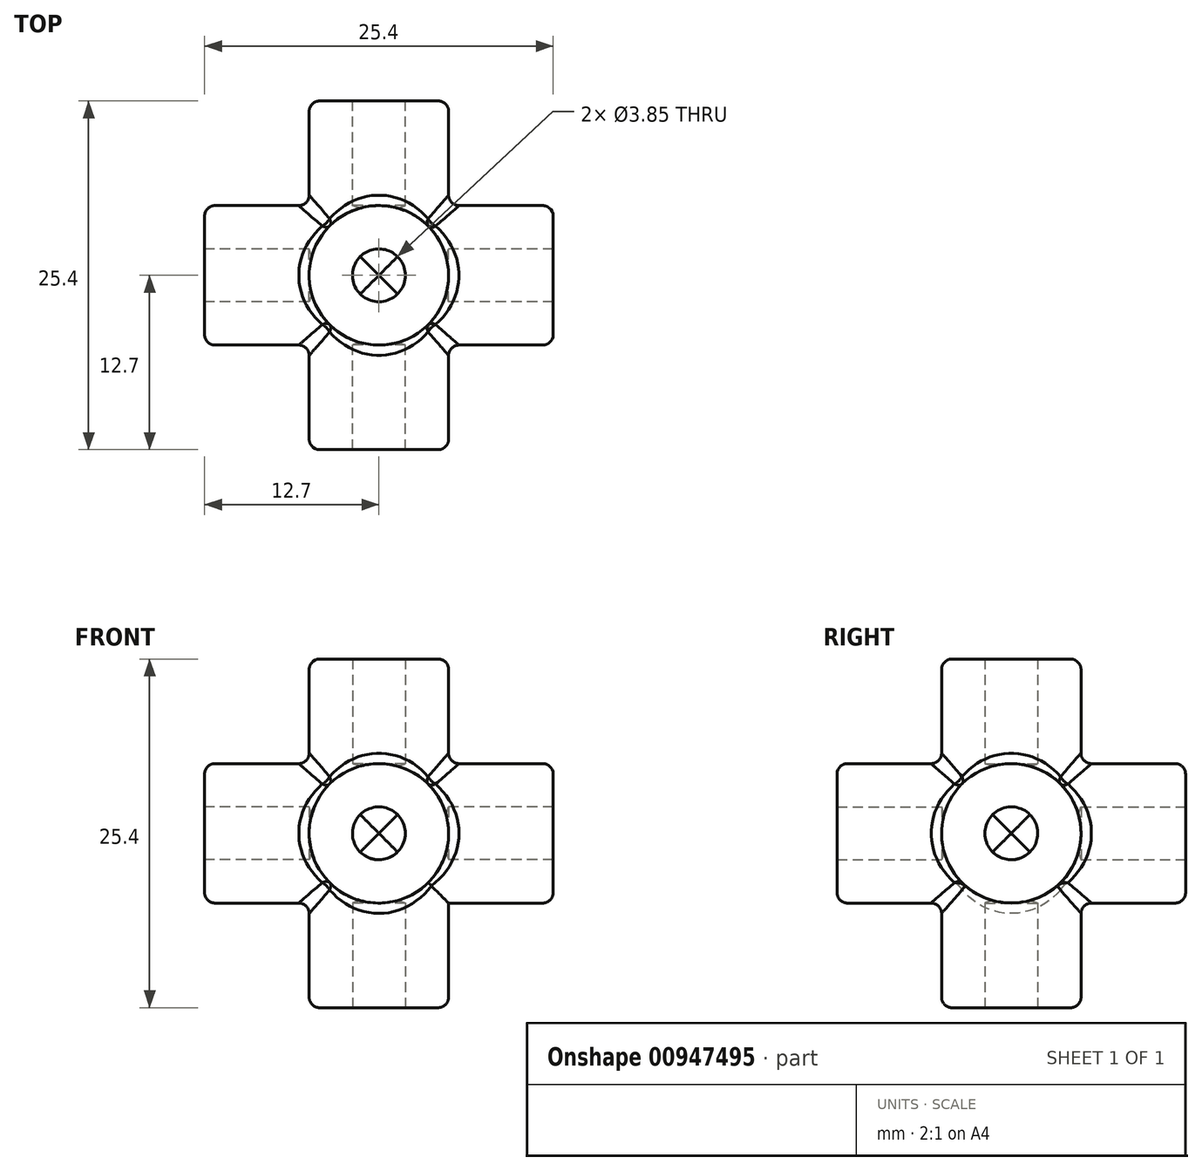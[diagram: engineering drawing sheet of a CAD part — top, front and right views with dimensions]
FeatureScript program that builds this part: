
annotation { "Feature Type Name" : "Feature", "Feature Type Description" : "" }
export const myFeature = defineFeature(function(context is Context, id is Id, definition is map)
    precondition{}
    {
        {
            var Q0;
            Q0=qCreatedBy(makeId("Front.planeOp"),FACE);
            var sketch = newSketch(context, id + "F0", { "sketchPlane" : qUnion([Q0])});
            skCircle(sketch, "E0", {"center": v(0, 0) * mm, "radius": 5.08 * mm});
            skCircle(sketch, "E1", {"center": v(0, 0) * mm, "radius": 1.92 * mm});
            skSolve(sketch);
        }
        {
            var Q0;
            Q0=makeQuery(id+"F0.imprint","IMPRINT",FACE,{"disambiguationData":[TD([[makeQuery(id+"F0.imprint","IMPRINT",EDGE,{"derivedFrom":sQuery(id+"F0.wireOp",EDGE,"E0")}),1.0]])]});
            extrude(context, id + "F1", {"entities" : qUnion([Q0]), "endBound" : BoundingType.SYMMETRIC, "depth" : 25.4 * mm, "offsetDistance" : 25.4 * mm});
        }
        {
            var Q0;
            Q0=qCreatedBy(makeId("Right.planeOp"),FACE);
            var sketch = newSketch(context, id + "F2", { "sketchPlane" : qUnion([Q0])});
            skCircle(sketch, "E2", {"center": v(0, 0) * mm, "radius": 1.92 * mm});
            skCircle(sketch, "E3", {"center": v(0, 0) * mm, "radius": 5.08 * mm});
            skSolve(sketch);
        }
        {
            var Q0;
            Q0=qCreatedBy(makeId("Top.planeOp"),FACE);
            var sketch = newSketch(context, id + "F3", { "sketchPlane" : qUnion([Q0])});
            skCircle(sketch, "E4", {"center": v(0, 0) * mm, "radius": 1.92 * mm});
            skCircle(sketch, "E5", {"center": v(0, 0) * mm, "radius": 5.08 * mm});
            skSolve(sketch);
        }
        {
            var Q0;
            Q0=qSketchRegion(id+"F2",true);
            extrude(context, id + "F4", {"entities" : qUnion([Q0]), "operationType" : NewBodyOperationType.ADD, "endBound" : BoundingType.SYMMETRIC, "depth" : 25.4 * mm, "offsetDistance" : 25.4 * mm});
        }
        {
            var Q0;
            Q0=makeQuery(id+"F3.imprint","IMPRINT",FACE,{"disambiguationData":[TD([[makeQuery(id+"F3.imprint","IMPRINT",EDGE,{"derivedFrom":sQuery(id+"F3.wireOp",EDGE,"E4")}),-1.0]])]});
            extrude(context, id + "F5", {"entities" : qUnion([Q0]), "operationType" : NewBodyOperationType.ADD, "endBound" : BoundingType.SYMMETRIC, "depth" : 25.4 * mm, "offsetDistance" : 25.4 * mm});
        }
        {
            var Q0;
            Q0=makeQuery(id+"F5.opExtrude","CAP_EDGE",EDGE,{"disambiguationData":[OSD([sQuery(id+"F3.wireOp",EDGE,"E5")])],"isStart":false});
            var Q1;
            Q1=makeQuery(id+"F1.opExtrude","CAP_EDGE",EDGE,{"disambiguationData":[OSD([sQuery(id+"F0.wireOp",EDGE,"E0")])],"isStart":false});
            var Q2;
            Q2=makeQuery(id+"F4.opExtrude","CAP_EDGE",EDGE,{"disambiguationData":[OSD([sQuery(id+"F2.wireOp",EDGE,"E3")])],"isStart":false});
            var Q3;
            Q3=makeQuery(id+"F1.opExtrude","CAP_EDGE",EDGE,{"disambiguationData":[OSD([sQuery(id+"F0.wireOp",EDGE,"E0")])],"isStart":true});
            var Q4;
            Q4=makeQuery(id+"F5.opExtrude","CAP_EDGE",EDGE,{"disambiguationData":[OSD([sQuery(id+"F3.wireOp",EDGE,"E5")])],"isStart":true});
            var Q5;
            Q5=makeQuery(id+"F4.opExtrude","CAP_EDGE",EDGE,{"disambiguationData":[OSD([sQuery(id+"F2.wireOp",EDGE,"E3")])],"isStart":true});
            var Q6;
            {var subQ0=sQuery(id+"F0.wireOp",EDGE,"E0");var subQ1=makeQuery(id+"F1.opExtrude","SWEPT_FACE",FACE,{"disambiguationData":[OSD([subQ0])]});Q6=makeQuery(id+"F5.boolean.opBoolean","INTERSECT",EDGE,{"disambiguationData":[OD(0.0)],"derivedFrom":[makeQuery(id+"F4.boolean.opBoolean","SPLIT",FACE,{"disambiguationData":[TD([subQ1,makeQuery(id+"F1.opExtrude","CAP_FACE",FACE,{"disambiguationData":[OSD([subQ0,sQuery(id+"F0.wireOp",EDGE,"E1")])],"isStart":true}),makeQuery(id+"F4.opExtrude","SWEPT_FACE",FACE,{"disambiguationData":[OSD([sQuery(id+"F2.wireOp",EDGE,"E3")])]})])],"derivedFrom":subQ1}),makeQuery(id+"F5.opExtrude","SWEPT_FACE",FACE,{"disambiguationData":[OSD([sQuery(id+"F3.wireOp",EDGE,"E5")])]})]});}
            var Q7;
            {var subQ0=sQuery(id+"F2.wireOp",EDGE,"E3");var subQ1=makeQuery(id+"F4.opExtrude","SWEPT_FACE",FACE,{"disambiguationData":[OSD([subQ0])]});Q7=makeQuery(id+"F5.boolean.opBoolean","INTERSECT",EDGE,{"disambiguationData":[OD(0.0)],"derivedFrom":[makeQuery(id+"F4.boolean.opBoolean","SPLIT",FACE,{"disambiguationData":[TD([makeQuery(id+"F1.opExtrude","SWEPT_FACE",FACE,{"disambiguationData":[OSD([sQuery(id+"F0.wireOp",EDGE,"E0")])]}),makeQuery(id+"F4.opExtrude","CAP_FACE",FACE,{"disambiguationData":[OSD([sQuery(id+"F2.wireOp",EDGE,"E2"),subQ0])],"isStart":true}),subQ1])],"derivedFrom":subQ1}),makeQuery(id+"F5.opExtrude","SWEPT_FACE",FACE,{"disambiguationData":[OSD([sQuery(id+"F3.wireOp",EDGE,"E5")])]})]});}
            var Q8;
            {var subQ0=makeQuery(id+"F1.opExtrude","SWEPT_FACE",FACE,{"disambiguationData":[OSD([sQuery(id+"F0.wireOp",EDGE,"E0")])]});var subQ1=makeQuery(id+"F4.opExtrude","SWEPT_FACE",FACE,{"disambiguationData":[OSD([sQuery(id+"F2.wireOp",EDGE,"E3")])]});Q8=makeQuery(id+"F5.boolean.opBoolean","SPLIT",EDGE,{"disambiguationData":[TD([subQ0,subQ1,makeQuery(id+"F5.opExtrude","SWEPT_FACE",FACE,{"disambiguationData":[OSD([sQuery(id+"F3.wireOp",EDGE,"E5")])]})])],"derivedFrom":makeQuery(id+"F4.boolean.opBoolean","INTERSECT",EDGE,{"disambiguationData":[OD(0.0)],"derivedFrom":[subQ0,subQ1]})});}
            var Q9;
            {var subQ0=makeQuery(id+"F1.opExtrude","SWEPT_FACE",FACE,{"disambiguationData":[OSD([sQuery(id+"F0.wireOp",EDGE,"E0")])]});var subQ1=makeQuery(id+"F4.opExtrude","SWEPT_FACE",FACE,{"disambiguationData":[OSD([sQuery(id+"F2.wireOp",EDGE,"E3")])]});Q9=makeQuery(id+"F5.boolean.opBoolean","SPLIT",EDGE,{"disambiguationData":[TD([subQ0,subQ1,makeQuery(id+"F5.opExtrude","SWEPT_FACE",FACE,{"disambiguationData":[OSD([sQuery(id+"F3.wireOp",EDGE,"E5")])]})])],"derivedFrom":makeQuery(id+"F4.boolean.opBoolean","INTERSECT",EDGE,{"disambiguationData":[OD(2.0)],"derivedFrom":[subQ0,subQ1]})});}
            var Q10;
            {var subQ0=sQuery(id+"F0.wireOp",EDGE,"E0");var subQ1=makeQuery(id+"F1.opExtrude","SWEPT_FACE",FACE,{"disambiguationData":[OSD([subQ0])]});Q10=makeQuery(id+"F5.boolean.opBoolean","INTERSECT",EDGE,{"disambiguationData":[OD(0.0)],"derivedFrom":[makeQuery(id+"F4.boolean.opBoolean","SPLIT",FACE,{"disambiguationData":[TD([subQ1,makeQuery(id+"F1.opExtrude","CAP_FACE",FACE,{"disambiguationData":[OSD([subQ0,sQuery(id+"F0.wireOp",EDGE,"E1")])],"isStart":false}),makeQuery(id+"F4.opExtrude","SWEPT_FACE",FACE,{"disambiguationData":[OSD([sQuery(id+"F2.wireOp",EDGE,"E3")])]})])],"derivedFrom":subQ1}),makeQuery(id+"F5.opExtrude","SWEPT_FACE",FACE,{"disambiguationData":[OSD([sQuery(id+"F3.wireOp",EDGE,"E5")])]})]});}
            var Q11;
            {var subQ0=sQuery(id+"F0.wireOp",EDGE,"E0");var subQ1=makeQuery(id+"F1.opExtrude","SWEPT_FACE",FACE,{"disambiguationData":[OSD([subQ0])]});Q11=makeQuery(id+"F5.boolean.opBoolean","INTERSECT",EDGE,{"disambiguationData":[OD(1.0)],"derivedFrom":[makeQuery(id+"F4.boolean.opBoolean","SPLIT",FACE,{"disambiguationData":[TD([subQ1,makeQuery(id+"F1.opExtrude","CAP_FACE",FACE,{"disambiguationData":[OSD([subQ0,sQuery(id+"F0.wireOp",EDGE,"E1")])],"isStart":false}),makeQuery(id+"F4.opExtrude","SWEPT_FACE",FACE,{"disambiguationData":[OSD([sQuery(id+"F2.wireOp",EDGE,"E3")])]})])],"derivedFrom":subQ1}),makeQuery(id+"F5.opExtrude","SWEPT_FACE",FACE,{"disambiguationData":[OSD([sQuery(id+"F3.wireOp",EDGE,"E5")])]})]});}
            var Q12;
            {var subQ0=makeQuery(id+"F1.opExtrude","SWEPT_FACE",FACE,{"disambiguationData":[OSD([sQuery(id+"F0.wireOp",EDGE,"E0")])]});var subQ1=makeQuery(id+"F4.opExtrude","SWEPT_FACE",FACE,{"disambiguationData":[OSD([sQuery(id+"F2.wireOp",EDGE,"E3")])]});Q12=makeQuery(id+"F5.boolean.opBoolean","SPLIT",EDGE,{"disambiguationData":[TD([subQ0,subQ1,makeQuery(id+"F5.opExtrude","SWEPT_FACE",FACE,{"disambiguationData":[OSD([sQuery(id+"F3.wireOp",EDGE,"E5")])]})])],"derivedFrom":makeQuery(id+"F4.boolean.opBoolean","INTERSECT",EDGE,{"disambiguationData":[OD(3.0)],"derivedFrom":[subQ0,subQ1]})});}
            var Q13;
            {var subQ0=sQuery(id+"F2.wireOp",EDGE,"E3");var subQ1=makeQuery(id+"F4.opExtrude","SWEPT_FACE",FACE,{"disambiguationData":[OSD([subQ0])]});Q13=makeQuery(id+"F5.boolean.opBoolean","INTERSECT",EDGE,{"disambiguationData":[OD(1.0)],"derivedFrom":[makeQuery(id+"F4.boolean.opBoolean","SPLIT",FACE,{"disambiguationData":[TD([makeQuery(id+"F1.opExtrude","SWEPT_FACE",FACE,{"disambiguationData":[OSD([sQuery(id+"F0.wireOp",EDGE,"E0")])]}),makeQuery(id+"F4.opExtrude","CAP_FACE",FACE,{"disambiguationData":[OSD([sQuery(id+"F2.wireOp",EDGE,"E2"),subQ0])],"isStart":false}),subQ1])],"derivedFrom":subQ1}),makeQuery(id+"F5.opExtrude","SWEPT_FACE",FACE,{"disambiguationData":[OSD([sQuery(id+"F3.wireOp",EDGE,"E5")])]})]});}
            var Q14;
            {var subQ0=makeQuery(id+"F1.opExtrude","SWEPT_FACE",FACE,{"disambiguationData":[OSD([sQuery(id+"F0.wireOp",EDGE,"E0")])]});var subQ1=makeQuery(id+"F4.opExtrude","SWEPT_FACE",FACE,{"disambiguationData":[OSD([sQuery(id+"F2.wireOp",EDGE,"E3")])]});Q14=makeQuery(id+"F5.boolean.opBoolean","SPLIT",EDGE,{"disambiguationData":[TD([subQ0,subQ1,makeQuery(id+"F5.opExtrude","SWEPT_FACE",FACE,{"disambiguationData":[OSD([sQuery(id+"F3.wireOp",EDGE,"E5")])]})])],"derivedFrom":makeQuery(id+"F4.boolean.opBoolean","INTERSECT",EDGE,{"disambiguationData":[OD(1.0)],"derivedFrom":[subQ0,subQ1]})});}
            var Q15;
            {var subQ0=sQuery(id+"F0.wireOp",EDGE,"E0");var subQ1=makeQuery(id+"F1.opExtrude","SWEPT_FACE",FACE,{"disambiguationData":[OSD([subQ0])]});Q15=makeQuery(id+"F5.boolean.opBoolean","INTERSECT",EDGE,{"disambiguationData":[OD(1.0)],"derivedFrom":[makeQuery(id+"F4.boolean.opBoolean","SPLIT",FACE,{"disambiguationData":[TD([subQ1,makeQuery(id+"F1.opExtrude","CAP_FACE",FACE,{"disambiguationData":[OSD([subQ0,sQuery(id+"F0.wireOp",EDGE,"E1")])],"isStart":true}),makeQuery(id+"F4.opExtrude","SWEPT_FACE",FACE,{"disambiguationData":[OSD([sQuery(id+"F2.wireOp",EDGE,"E3")])]})])],"derivedFrom":subQ1}),makeQuery(id+"F5.opExtrude","SWEPT_FACE",FACE,{"disambiguationData":[OSD([sQuery(id+"F3.wireOp",EDGE,"E5")])]})]});}
            var Q16;
            {var subQ0=sQuery(id+"F2.wireOp",EDGE,"E3");var subQ1=makeQuery(id+"F4.opExtrude","SWEPT_FACE",FACE,{"disambiguationData":[OSD([subQ0])]});Q16=makeQuery(id+"F5.boolean.opBoolean","INTERSECT",EDGE,{"disambiguationData":[OD(1.0)],"derivedFrom":[makeQuery(id+"F4.boolean.opBoolean","SPLIT",FACE,{"disambiguationData":[TD([makeQuery(id+"F1.opExtrude","SWEPT_FACE",FACE,{"disambiguationData":[OSD([sQuery(id+"F0.wireOp",EDGE,"E0")])]}),makeQuery(id+"F4.opExtrude","CAP_FACE",FACE,{"disambiguationData":[OSD([sQuery(id+"F2.wireOp",EDGE,"E2"),subQ0])],"isStart":true}),subQ1])],"derivedFrom":subQ1}),makeQuery(id+"F5.opExtrude","SWEPT_FACE",FACE,{"disambiguationData":[OSD([sQuery(id+"F3.wireOp",EDGE,"E5")])]})]});}
            fillet(context, id + "F6", {"entities" : qUnion([Q0, Q1, Q2, Q3, Q4, Q5, Q6, Q7, Q8, Q9, Q10, Q11, Q12, Q13, Q14, Q15, Q16]), "radius" : 0.76 * mm, "tangentPropagation" : true, "allowEdgeOverflow" : false});
        }
    });
